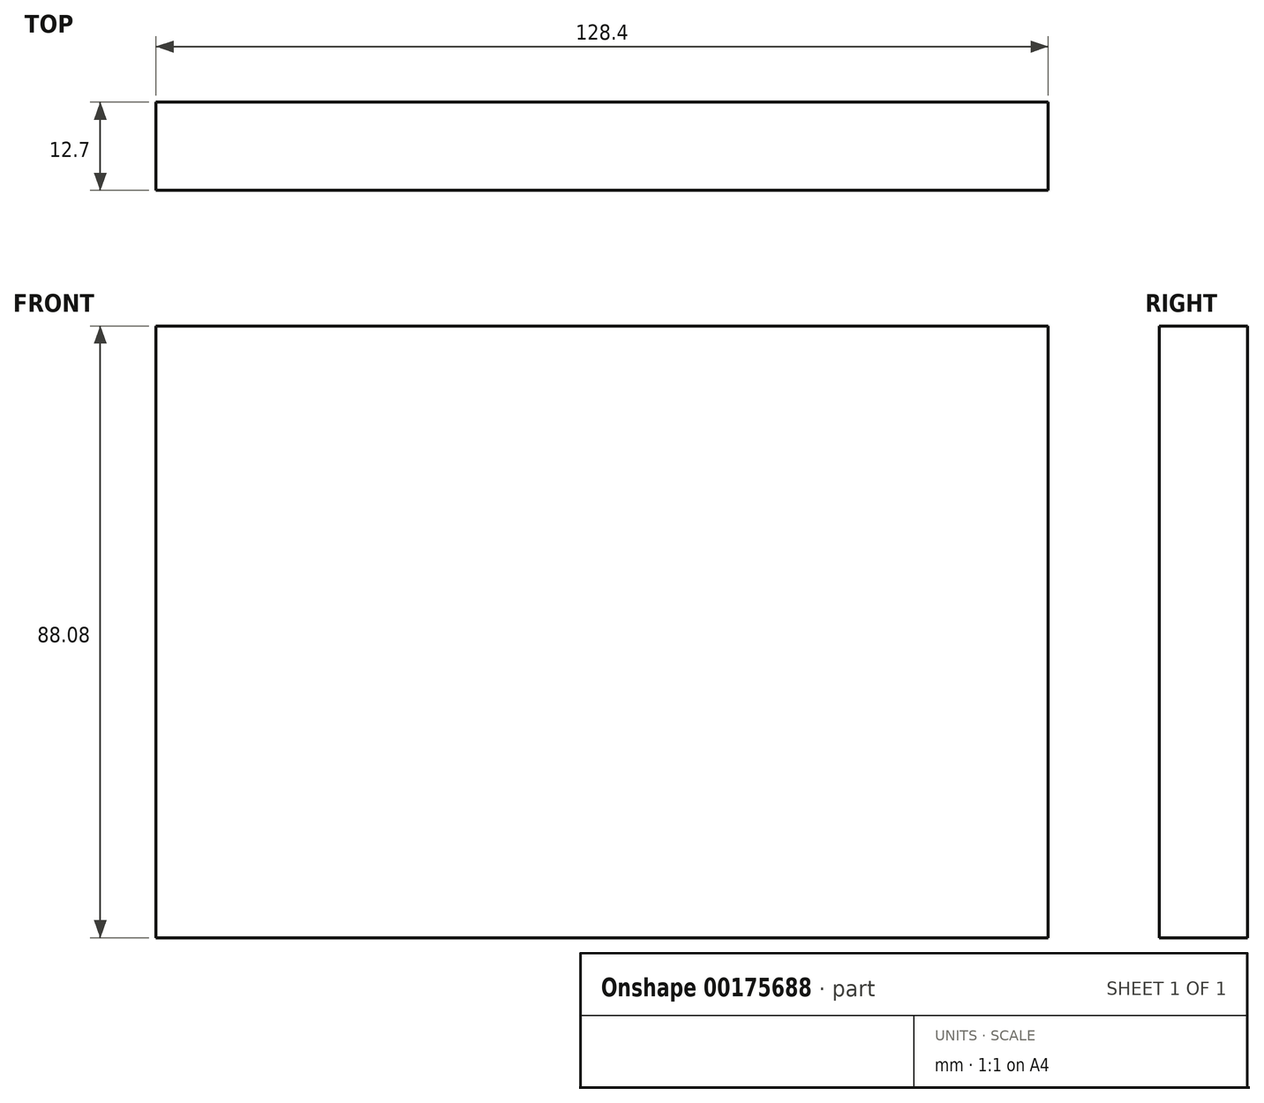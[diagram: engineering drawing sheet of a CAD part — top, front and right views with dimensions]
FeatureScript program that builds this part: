
annotation { "Feature Type Name" : "Feature", "Feature Type Description" : "" }
export const myFeature = defineFeature(function(context is Context, id is Id, definition is map)
    precondition{}
    {
        {
            var Q0;
            Q0=qCreatedBy(makeId("Front.planeOp"),FACE);
            var sketch = newSketch(context, id + "F0", { "sketchPlane" : qUnion([Q0])});
            skLineSegment(sketch, "E0.bottom", {"start": v(64.2, 44.04) * mm, "end": v(-64.2, 44.04) * mm});
            skLineSegment(sketch, "E0.top", {"start": v(64.2, -44.04) * mm, "end": v(-64.2, -44.04) * mm});
            skLineSegment(sketch, "E0.left", {"start": v(64.2, 44.04) * mm, "end": v(64.2, -44.04) * mm});
            skLineSegment(sketch, "E0.right", {"start": v(-64.2, 44.04) * mm, "end": v(-64.2, -44.04) * mm});
            skPoint(sketch, "E0.middle", {"position": v(0, 0) * mm});
            skSolve(sketch);
        }
        {
            var Q0;
            Q0 = qSketchRegion(id + "F0", true);
            extrude(context, id + "F1", {"entities" : qUnion([Q0]), "depth" : 12.7 * mm});
        }
    });
